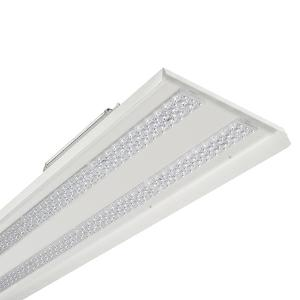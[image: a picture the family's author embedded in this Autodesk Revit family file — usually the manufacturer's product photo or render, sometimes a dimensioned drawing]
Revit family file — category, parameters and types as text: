
# Revit family: 3f_filippi_-_kit_led_retrofit_beta_430_2x_3f_filippi_-_a5308_-_kit_led_beta_430_-_l1551-_2x65w_ampio
name_source: partatom
category: Lighting Fixtures
units: mm (PartAtom-declared; Revit-internal decimal feet)

## family parameters
Cut with Voids When Loaded = No
Host = Face
Light Source = No
Part Type = Normal
Room Calculation Point = No
Round Connector Dimension = Use Diameter
Shared = No

## types (1)
- 3F Filippi - Kit LED Retrofit Beta 430 2X (1 x LED, 19205 lm, 120 W, 4000 K)
    Apparent Load = 120 VA
    Approval mark = ENEC
    CIE Flux Codes = 63 95 100 100 100
    Color Rendering = 80
    Color Temperature = 4000 K
    Control Gear = Electronic ballast
    Default Elevation = 1800 mm
    Description = Beta 430 Retrofit Kit to replace the 4x49W T5 Amalgam or the 4x58W T8 version

ILLUMINOTECHNICAL
Luminous efficiency 100% (DLOR 100%, ULOR 0%).
Initial luminous flux of the luminaire 19205 lm.
Wide symmetric distribution.
Installation Interdistance Transv.D = 1.49 x hu - Long.D = 1.54 x hu.
Tabular UGR (CIE 117 - 4H-8H; S=0.25H; 70/50/20): RUG 19.3 - 19.8.
Beam angle: 100° - 100°.
Luminous efficacy 160 lm/W.
Lifetime (L93/B10): 30000 h. (tq+25°C)
Lifetime (L90/B10): 50000 h. (tq+25°C)
Lifetime (L85/B10): 80000 h. (tq+25°C)
Lifetime (L80/B10): 100000 h. (tq+25°C)
Lifetime (L85/B10): 50000 h. (tq+40°C)
Sudden decreased luminous flux after 50000 hours: 0% (C0).
Photobiological safety in compliance with IEC/TR 62778: RG0 risk exempt, (IEC 62471).
In compliance with IEC/EN 62722-2-1 - IEC/EN 62717 standards.

SOURCE
2 linear LED modules 65W/840.
Energy efficiency class (UE 2019/2020 - UE 2019/2015): C.
CIE 13.3 Colour rendering index: CRI >80 (R9 <50%).
IES TM-30 Fidelity Index: Rf = 84 Rg = 95.
CCT nominal colour temperature 4000 K.
Colour initial tolerance (MacAdam): SDCM 3.

MECHANICAL
Gear-tray unit hot-galvanised steel, painted in white polyester.
Methacrylate (PMMA) lenses with external flat surface.
Luminaire with limited surface temperature. - D - (EN 60598-2-24)
Dimensions: 1551x430 mm, height 159 mm. Weight 5.417 kg.
Glow-wire test resistance 850°C.

ELECTRICAL
Halogen Free electronic wiring 230V-50/60Hz, power factor 0.97, THD <25%, constant output current, class I, 2 driver.
Twin-circuit.
Power of the luminaire 120 W.
CE - IEC 60598-1 - EN 60598-1.
SAFE FLICKER: PstLM=<1 and SVM=<0.4 (IEC TR 61547-1 and IEC TR 63158), to ensure a more comfortable and safe light.
Luminaire compliant with EN 60598-2-22 for power supply from a centralised emergency system CPSS (Central Power Supply System), not incorporated in the luminaire - high risk areas excluded. The default power and flux are 100% in AC and 100% in DC.
Ambient temperature from -20°C to +40°C.
Temperature class T6 max 85°C.
Relative humidity UR: <85%.

INSTALLATION
Retrofit.
Correct installation of the retrofit LED kit, compliant with EN 60598-1 and CE marked, inside the 3F Filippi - Beta 4x and 6x i3F 76 Fluorescent luminaires must be only carried out by qualified personnel to ensure compliance with the national installation standards.
Attention: to maintain the degree of protection of the device and for the purposes of validity of the guarantee of the new retrofit kits, it is imperative to replace the old cable guides (on the body of the device) with the new ones supplied.
All accessories dedicated to this product are available on the Catalog and on our website www.3F-Filippi.com.

WARNING
Fixture not suitable for cold stores with an ambient temperature <0°C and/or relative humidity >85%.
Luminaire designed for disposal/recycling at end-of-life.
Replaceable (LED only) light source by a professional. Replaceable control gear by a professional.
    Height = 159 mm
    Lamp = 1 x LED
    Lamp Light Flux = 19205 lm
    Lamp Power = 120 W
    Lamp count = 1
    Length = 1551 mm
    Lifetime = 50000 h
    Luminous efficacy = 160 lm/W
    Manufacturer = 3F Filippi
    ModVariant = No
    Model = 3F Filippi - A5308 - Kit LED Beta 430 - L1551- 2X65W AMPIO
    Mounting Place = Ceiling
    Mounting Type = Surface mounted
    Number of Poles = 1
    OnlyDefault = Yes
    Power Factor = 1
    Product Name = 3F Filippi - Kit LED Retrofit Beta 430 2X
    Product group = ceiling mounted luminaire
    ProductGroupID = 3
    Protection Class = Protection class I
    Protection Degree = Degree of protection
    RLX_Detail_Level = 1
    RLX_Emergency_Light_Flux = 0 lm
    RLX_Emergency_Type = 0
    RLX_Emergency_Type_DB = No
    RlxData = <blob elided: 69541 chars, md5=64996752>
    Socket = socket
    Standby Power = 0 W
    System Light Flux = 19205 lm
    System Power = 120 W
    Type Comments = Product without accessories
    Type Image = 3ffilippi_a5308.jpg
    URL = http://relux.com
    VarID = ---
    Voltage = 0 V
    Weight = 0.00 kg
    Width = 430 mm

## geometry (parser evidence)
native form markers: Blend x4, Sweep x9
no freeform markers — native parametric forms only
